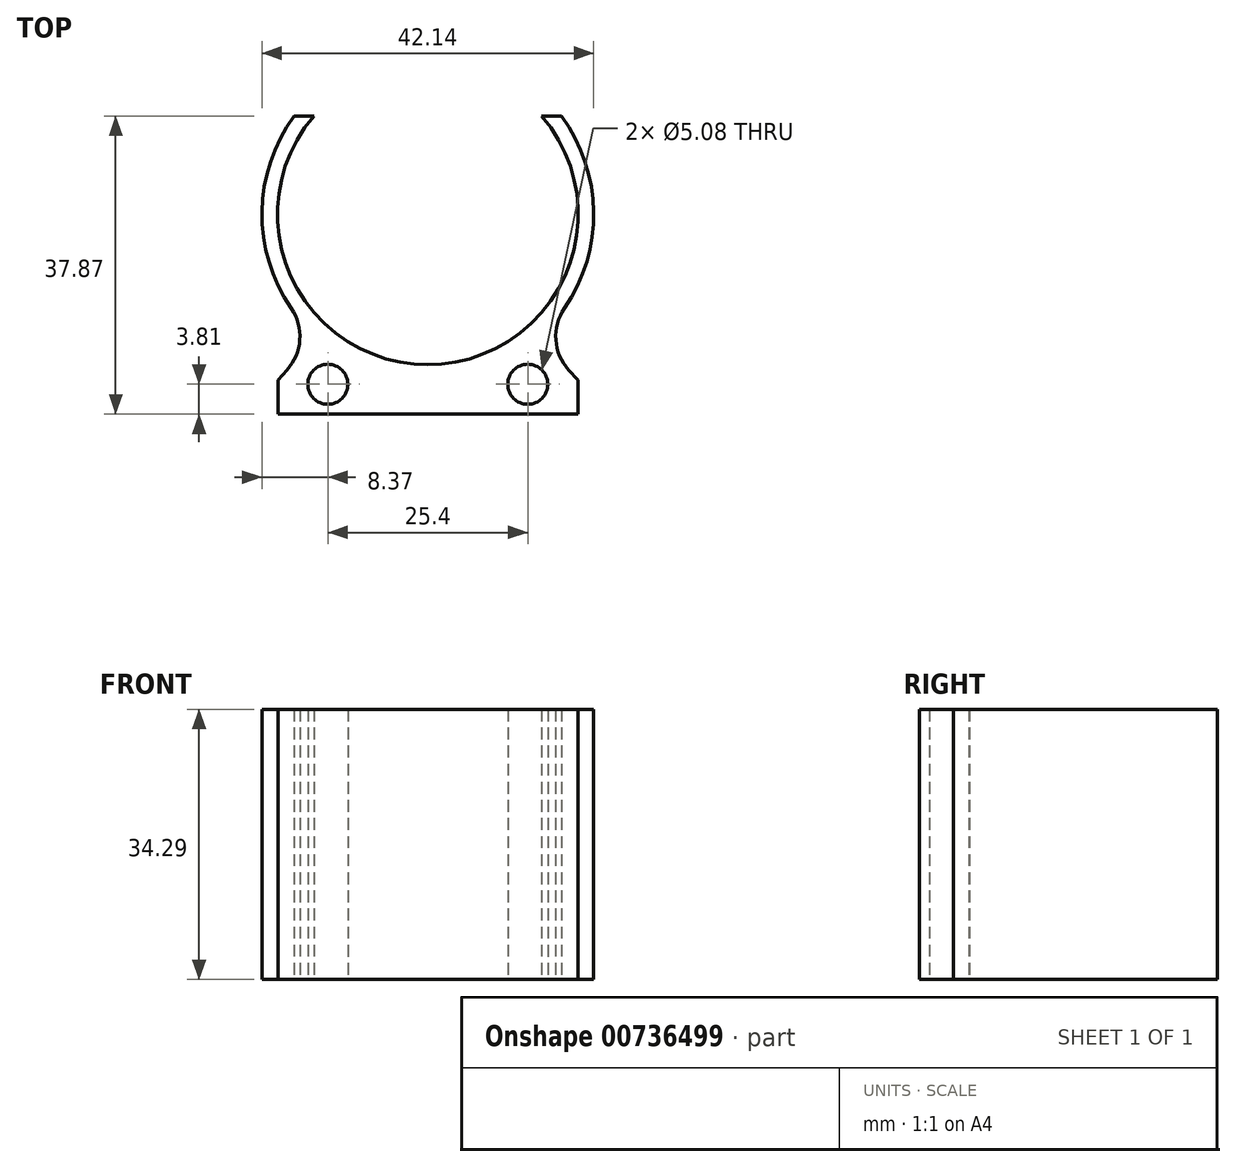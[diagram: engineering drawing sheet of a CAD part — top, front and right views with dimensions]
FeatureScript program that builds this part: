
annotation { "Feature Type Name" : "Feature", "Feature Type Description" : "" }
export const myFeature = defineFeature(function(context is Context, id is Id, definition is map)
    precondition{}
    {
        {
            var Q0;
            Q0=qCreatedBy(makeId("Top.planeOp"),FACE);
            var sketch = newSketch(context, id + "F0", { "sketchPlane" : qUnion([Q0])});
            skArc(sketch, "E0", {"start": v(-16.98, 12.47) * mm, "mid": v(-21.07, 0.33) * mm, "end": v(-17.37, -11.93) * mm});
            skLineSegment(sketch, "E1.0", {"start": v(-16.98, 12.47) * mm, "end": v(-14.47, 12.47) * mm});
            skLineSegment(sketch, "E2.trimOffspring", {"start": v(14.47, 12.47) * mm, "end": v(16.98, 12.47) * mm});
            skPoint(sketch, "E3.orphan", {"position": v(-32.43, 0) * mm});
            skLineSegment(sketch, "E4.0", {"start": v(-19.05, -25.4) * mm, "end": v(0, -25.4) * mm});
            skLineSegment(sketch, "E5.0", {"start": v(-19.05, -21.07) * mm, "end": v(-19.05, -25.4) * mm});
            skLineSegment(sketch, "E6", {"start": v(-19.05, -21.07) * mm, "end": v(-17.89, -19.79) * mm});
            skPoint(sketch, "E7.visualSharp", {"position": v(-14.13, -15.63) * mm});
            skArc(sketch, "E7.filletArc", {"start": v(-17.89, -19.79) * mm, "mid": v(-16.26, -15.95) * mm, "end": v(-17.37, -11.93) * mm});
            skArc(sketch, "E8.MirrorCS", {"start": v(17.89, -19.79) * mm, "mid": v(16.26, -15.95) * mm, "end": v(17.37, -11.93) * mm});
            skLineSegment(sketch, "E9.MirrorCS", {"start": v(19.05, -21.07) * mm, "end": v(17.89, -19.79) * mm});
            skLineSegment(sketch, "E10.MirrorCS", {"start": v(19.05, -21.07) * mm, "end": v(19.05, -25.4) * mm});
            skLineSegment(sketch, "E11.MirrorCS", {"start": v(19.05, -25.4) * mm, "end": v(0, -25.4) * mm});
            skArc(sketch, "E12.MirrorCS", {"start": v(16.98, 12.47) * mm, "mid": v(21.07, 0.33) * mm, "end": v(17.37, -11.93) * mm});
            skCircle(sketch, "E13", {"center": v(12.7, -21.59) * mm, "radius": 2.54 * mm});
            skCircle(sketch, "E14.MirrorC", {"center": v(-12.7, -21.59) * mm, "radius": 2.54 * mm});
            skArc(sketch, "E15.0", {"start": v(-14.47, 12.47) * mm, "mid": v(0, -19.1) * mm, "end": v(14.47, 12.47) * mm});
            skSolve(sketch);
        }
        {
            var Q0;
            Q0=makeQuery(id+"F0.imprint","IMPRINT",FACE,{"disambiguationData":[TD([[makeQuery(id+"F0.imprint","IMPRINT",EDGE,{"derivedFrom":sQuery(id+"F0.wireOp",EDGE,"E0")}),1.0]])]});
            extrude(context, id + "F1", {"entities" : qUnion([Q0]), "depth" : 34.3 * mm, "offsetDistance" : 25.4 * mm});
        }
    });
